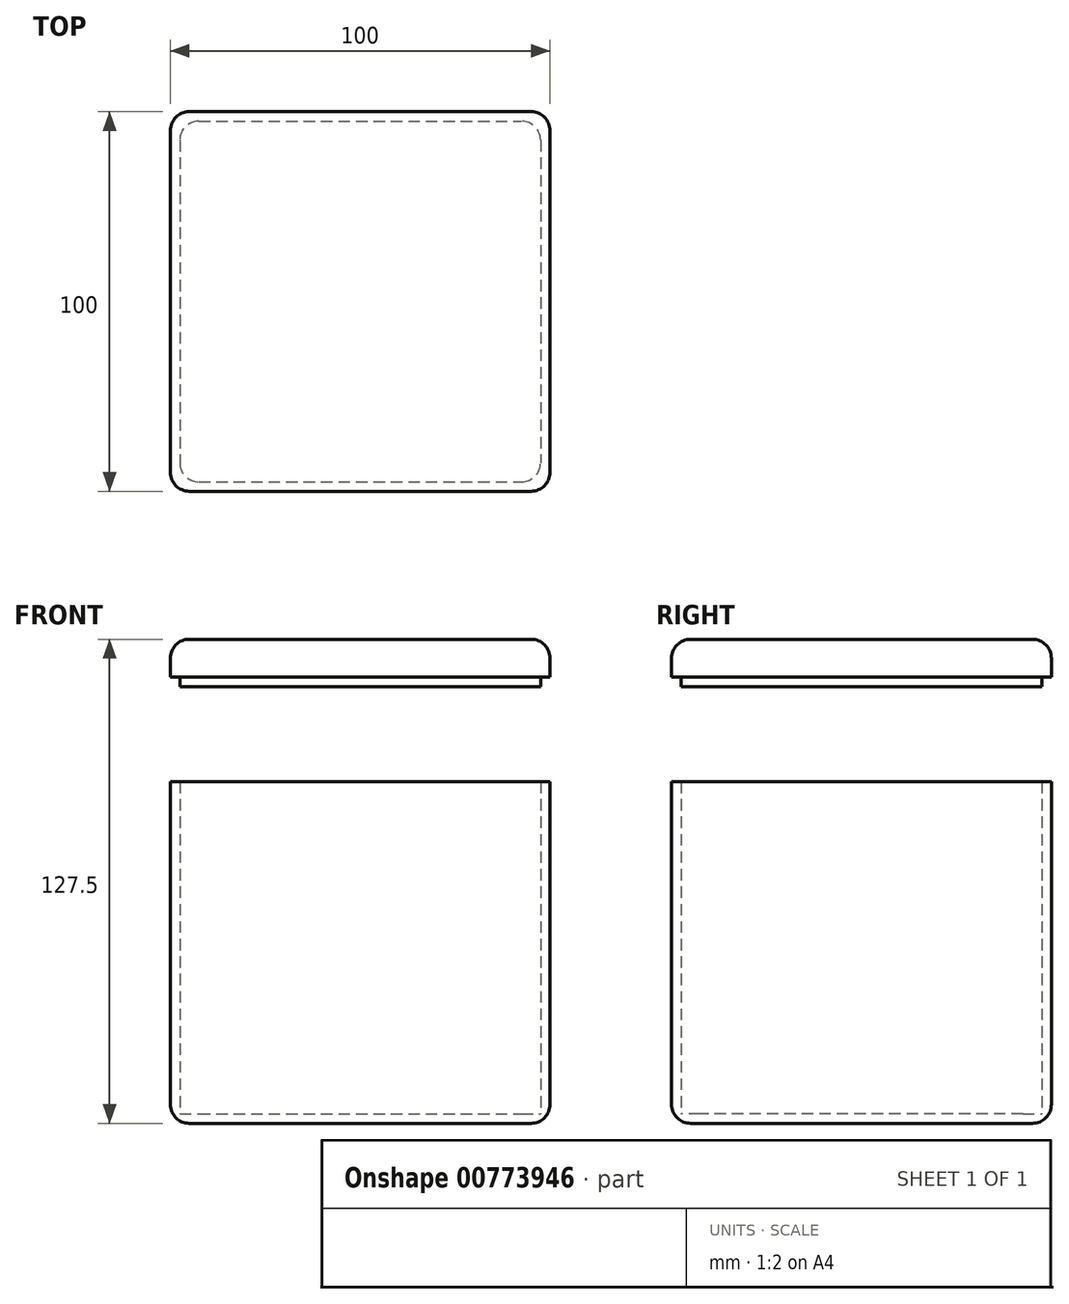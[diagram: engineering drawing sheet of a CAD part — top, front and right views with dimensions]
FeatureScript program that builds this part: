
annotation { "Feature Type Name" : "Feature", "Feature Type Description" : "" }
export const myFeature = defineFeature(function(context is Context, id is Id, definition is map)
    precondition{}
    {
        {
            var Q0;
            Q0=qCreatedBy(makeId("Top.planeOp"),FACE);
            var sketch = newSketch(context, id + "F0", { "sketchPlane" : qUnion([Q0])});
            skLineSegment(sketch, "E0.bottom", {"start": v(-50, 50) * mm, "end": v(50, 50) * mm});
            skLineSegment(sketch, "E0.top", {"start": v(-50, -50) * mm, "end": v(50, -50) * mm});
            skLineSegment(sketch, "E0.left", {"start": v(-50, 50) * mm, "end": v(-50, -50) * mm});
            skLineSegment(sketch, "E0.right", {"start": v(50, 50) * mm, "end": v(50, -50) * mm});
            skSolve(sketch);
        }
        {
            var Q0;
            Q0=makeQuery(id+"F0.imprint","IMPRINT",FACE,{"disambiguationData":[TD([[makeQuery(id+"F0.imprint","IMPRINT",EDGE,{"derivedFrom":sQuery(id+"F0.wireOp",EDGE,"E0.bottom")}),-1.0]])]});
            extrude(context, id + "F1", {"entities" : qUnion([Q0]), "depth" : 90 * mm, "offsetDistance" : 25 * mm});
        }
        {
            var Q0;
            Q0=makeQuery(id+"F1.opExtrude","CAP_FACE",FACE,{"disambiguationData":[OSD([sQuery(id+"F0.wireOp",EDGE,"E0.bottom"),sQuery(id+"F0.wireOp",EDGE,"E0.top"),sQuery(id+"F0.wireOp",EDGE,"E0.left"),sQuery(id+"F0.wireOp",EDGE,"E0.right")])],"isStart":false});
            shell(context, id + "F2", {"entities" : qUnion([Q0]), "thickness" : 2.5 * mm});
        }
        {
            var Q0;
            Q0=makeQuery(id+"F1.opExtrude","CAP_FACE",FACE,{"disambiguationData":[OSD([sQuery(id+"F0.wireOp",EDGE,"E0.bottom"),sQuery(id+"F0.wireOp",EDGE,"E0.top"),sQuery(id+"F0.wireOp",EDGE,"E0.left"),sQuery(id+"F0.wireOp",EDGE,"E0.right")])],"isStart":false});
            cPlane(context, id + "F3", {"entities" : qUnion([Q0]), "cplaneType" : CPlaneType.OFFSET, "offset" : 25 * mm, "width" : 150 * mm, "height" : 150 * mm});
        }
        {
            var Q0;
            Q0=qCreatedBy(id+"F3.planeOp",FACE);
            var sketch = newSketch(context, id + "F4", { "sketchPlane" : qUnion([Q0])});
            skLineSegment(sketch, "E1.bottom", {"start": v(-47.5, 47.5) * mm, "end": v(47.5, 47.5) * mm});
            skLineSegment(sketch, "E1.top", {"start": v(-47.5, -47.5) * mm, "end": v(47.5, -47.5) * mm});
            skLineSegment(sketch, "E1.left", {"start": v(-47.5, 47.5) * mm, "end": v(-47.5, -47.5) * mm});
            skLineSegment(sketch, "E1.right", {"start": v(47.5, 47.5) * mm, "end": v(47.5, -47.5) * mm});
            skSolve(sketch);
        }
        {
            var Q0;
            Q0=makeQuery(id+"F4.imprint","IMPRINT",FACE,{"disambiguationData":[TD([[makeQuery(id+"F4.imprint","IMPRINT",EDGE,{"derivedFrom":sQuery(id+"F4.wireOp",EDGE,"E1.bottom")}),-1.0]])]});
            extrude(context, id + "F5", {"entities" : qUnion([Q0]), "depth" : 2.5 * mm, "offsetDistance" : 25 * mm});
        }
        {
            var Q0;
            Q0=makeQuery(id+"F5.opExtrude","CAP_FACE",FACE,{"disambiguationData":[OSD([sQuery(id+"F4.wireOp",EDGE,"E1.bottom"),sQuery(id+"F4.wireOp",EDGE,"E1.top"),sQuery(id+"F4.wireOp",EDGE,"E1.left"),sQuery(id+"F4.wireOp",EDGE,"E1.right")])],"isStart":false});
            var sketch = newSketch(context, id + "F6", { "sketchPlane" : qUnion([Q0])});
            skLineSegment(sketch, "E2.bottom", {"start": v(-50, 50) * mm, "end": v(50, 50) * mm});
            skLineSegment(sketch, "E2.top", {"start": v(-50, -50) * mm, "end": v(50, -50) * mm});
            skLineSegment(sketch, "E2.left", {"start": v(-50, 50) * mm, "end": v(-50, -50) * mm});
            skLineSegment(sketch, "E2.right", {"start": v(50, 50) * mm, "end": v(50, -50) * mm});
            skSolve(sketch);
        }
        {
            var Q0;
            Q0 = qSketchRegion(id + "F6", true);
            extrude(context, id + "F7", {"entities" : qUnion([Q0]), "operationType" : NewBodyOperationType.ADD, "depth" : 10 * mm, "offsetDistance" : 25 * mm});
        }
        {
            var Q0;
            Q0=makeQuery(id+"F1.opExtrude","SWEPT_EDGE",EDGE,{"disambiguationData":[OSD([sQuery(id+"F0.wireOp",EDGE,"E0.bottom"),sQuery(id+"F0.wireOp",EDGE,"E0.right")])]});
            var Q1;
            Q1=makeQuery(id+"F7.opExtrude","SWEPT_EDGE",EDGE,{"disambiguationData":[OSD([sQuery(id+"F6.wireOp",EDGE,"E2.bottom"),sQuery(id+"F6.wireOp",EDGE,"E2.right")])]});
            var Q2;
            Q2=makeQuery(id+"F7.opExtrude","SWEPT_EDGE",EDGE,{"disambiguationData":[OSD([sQuery(id+"F6.wireOp",EDGE,"E2.bottom"),sQuery(id+"F6.wireOp",EDGE,"E2.left")])]});
            var Q3;
            Q3=makeQuery(id+"F1.opExtrude","SWEPT_EDGE",EDGE,{"disambiguationData":[OSD([sQuery(id+"F0.wireOp",EDGE,"E0.bottom"),sQuery(id+"F0.wireOp",EDGE,"E0.left")])]});
            var Q4;
            Q4=makeQuery(id+"F7.opExtrude","SWEPT_EDGE",EDGE,{"disambiguationData":[OSD([sQuery(id+"F6.wireOp",EDGE,"E2.top"),sQuery(id+"F6.wireOp",EDGE,"E2.left")])]});
            var Q5;
            Q5=makeQuery(id+"F1.opExtrude","SWEPT_EDGE",EDGE,{"disambiguationData":[OSD([sQuery(id+"F0.wireOp",EDGE,"E0.top"),sQuery(id+"F0.wireOp",EDGE,"E0.left")])]});
            var Q6;
            Q6=makeQuery(id+"F7.opExtrude","SWEPT_EDGE",EDGE,{"disambiguationData":[OSD([sQuery(id+"F6.wireOp",EDGE,"E2.top"),sQuery(id+"F6.wireOp",EDGE,"E2.right")])]});
            var Q7;
            Q7=makeQuery(id+"F1.opExtrude","SWEPT_EDGE",EDGE,{"disambiguationData":[OSD([sQuery(id+"F0.wireOp",EDGE,"E0.top"),sQuery(id+"F0.wireOp",EDGE,"E0.right")])]});
            var Q8;
            Q8=makeQuery(id+"F7.opExtrude","CAP_FACE",FACE,{"disambiguationData":[OSD([sQuery(id+"F6.wireOp",EDGE,"E2.bottom"),sQuery(id+"F6.wireOp",EDGE,"E2.top"),sQuery(id+"F6.wireOp",EDGE,"E2.left"),sQuery(id+"F6.wireOp",EDGE,"E2.right")])],"isStart":false});
            var Q9;
            Q9=makeQuery(id+"F1.opExtrude","CAP_FACE",FACE,{"disambiguationData":[OSD([sQuery(id+"F0.wireOp",EDGE,"E0.bottom"),sQuery(id+"F0.wireOp",EDGE,"E0.top"),sQuery(id+"F0.wireOp",EDGE,"E0.left"),sQuery(id+"F0.wireOp",EDGE,"E0.right")])],"isStart":true});
            fillet(context, id + "F8", {"entities" : qUnion([Q0, Q1, Q2, Q3, Q4, Q5, Q6, Q7, Q8, Q9]), "radius" : 5 * mm, "tangentPropagation" : true, "allowEdgeOverflow" : false});
        }
        {
            var Q0;
            Q0=makeQuery(id+"F2.opShell","OFFSET_EDGE",EDGE,{"disambiguationData":[OSD([sQuery(id+"F0.wireOp",EDGE,"E0.bottom"),sQuery(id+"F0.wireOp",EDGE,"E0.left")])]});
            var Q1;
            Q1=makeQuery(id+"F2.opShell","OFFSET_EDGE",EDGE,{"disambiguationData":[OSD([sQuery(id+"F0.wireOp",EDGE,"E0.bottom"),sQuery(id+"F0.wireOp",EDGE,"E0.right")])]});
            var Q2;
            Q2=makeQuery(id+"F2.opShell","OFFSET_EDGE",EDGE,{"disambiguationData":[OSD([sQuery(id+"F0.wireOp",EDGE,"E0.top"),sQuery(id+"F0.wireOp",EDGE,"E0.right")])]});
            var Q3;
            Q3=makeQuery(id+"F2.opShell","OFFSET_EDGE",EDGE,{"disambiguationData":[OSD([sQuery(id+"F0.wireOp",EDGE,"E0.top"),sQuery(id+"F0.wireOp",EDGE,"E0.left")])]});
            var Q4;
            Q4=makeQuery(id+"F5.opExtrude","SWEPT_EDGE",EDGE,{"disambiguationData":[OSD([sQuery(id+"F4.wireOp",EDGE,"E1.bottom"),sQuery(id+"F4.wireOp",EDGE,"E1.right")])]});
            var Q5;
            Q5=makeQuery(id+"F5.opExtrude","SWEPT_EDGE",EDGE,{"disambiguationData":[OSD([sQuery(id+"F4.wireOp",EDGE,"E1.top"),sQuery(id+"F4.wireOp",EDGE,"E1.right")])]});
            var Q6;
            Q6=makeQuery(id+"F5.opExtrude","SWEPT_EDGE",EDGE,{"disambiguationData":[OSD([sQuery(id+"F4.wireOp",EDGE,"E1.top"),sQuery(id+"F4.wireOp",EDGE,"E1.left")])]});
            var Q7;
            Q7=makeQuery(id+"F5.opExtrude","SWEPT_EDGE",EDGE,{"disambiguationData":[OSD([sQuery(id+"F4.wireOp",EDGE,"E1.bottom"),sQuery(id+"F4.wireOp",EDGE,"E1.left")])]});
            fillet(context, id + "F9", {"entities" : qUnion([Q0, Q1, Q2, Q3, Q4, Q5, Q6, Q7]), "radius" : 5 * mm, "tangentPropagation" : true, "allowEdgeOverflow" : false});
        }
    });
